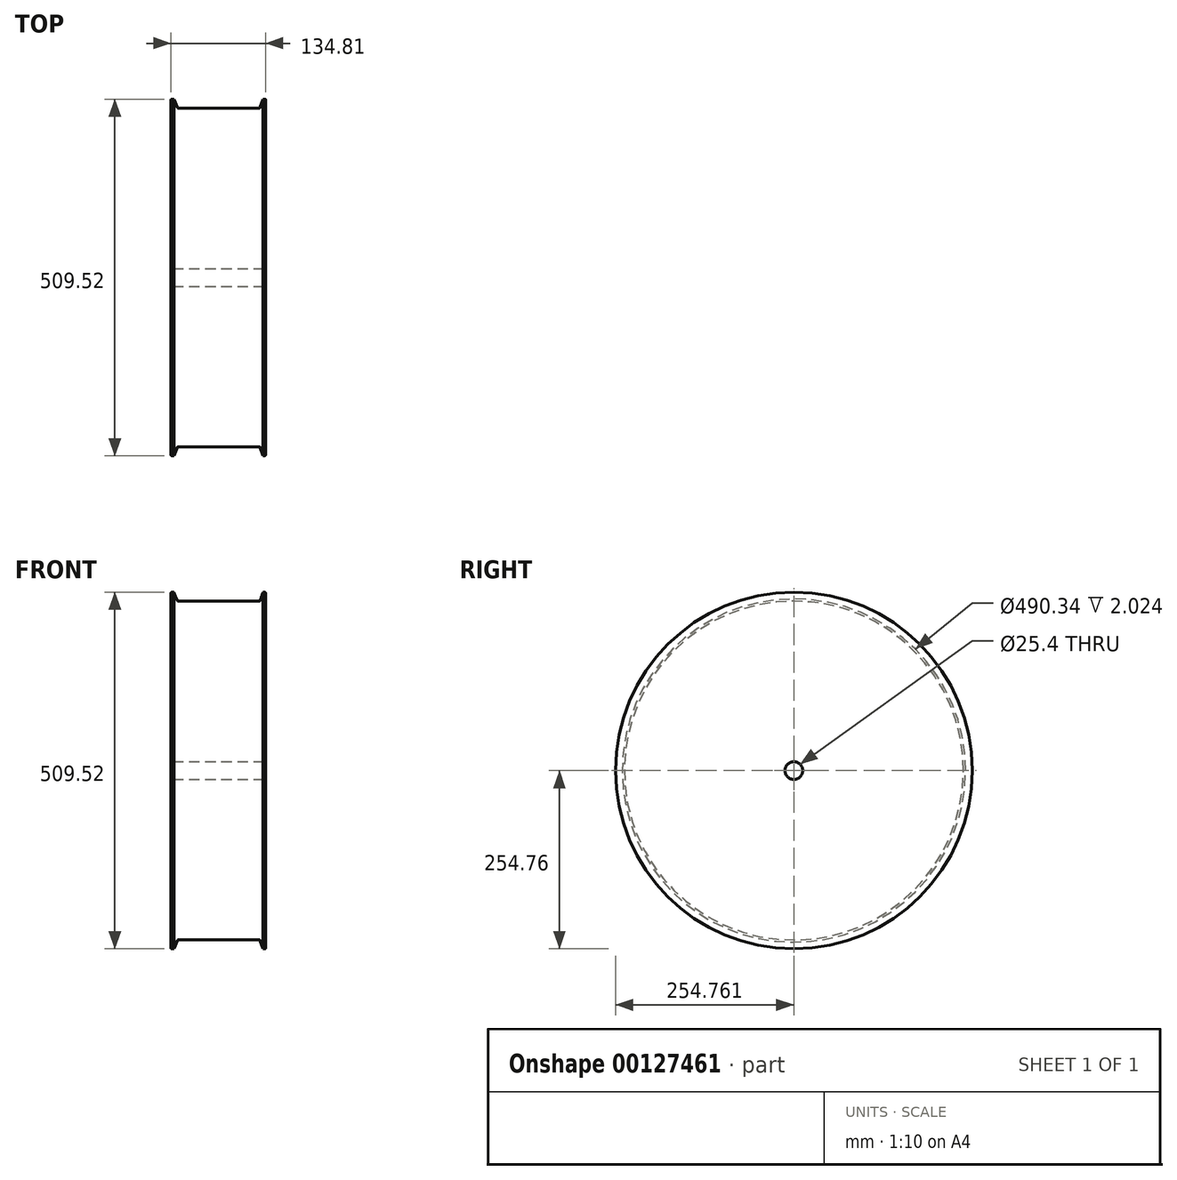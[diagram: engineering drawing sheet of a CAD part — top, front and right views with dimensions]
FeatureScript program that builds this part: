
annotation { "Feature Type Name" : "Feature", "Feature Type Description" : "" }
export const myFeature = defineFeature(function(context is Context, id is Id, definition is map)
    precondition{}
    {
        {
            var Q0;
            Q0=qCreatedBy(makeId("Top.planeOp"),FACE);
            var sketch = newSketch(context, id + "F0", { "sketchPlane" : qUnion([Q0])});
            skLineSegment(sketch, "E0", {"start": v(-3.62, 20.48) * mm, "end": v(-3.62, 29.09) * mm});
            skLineSegment(sketch, "E1", {"start": v(-2.86, 29.85) * mm, "end": v(0.66, 29.85) * mm});
            skLineSegment(sketch, "E2", {"start": v(0.66, 29.85) * mm, "end": v(5.74, 17.62) * mm});
            skArc(sketch, "E3.filletArc", {"start": v(-2.86, 29.85) * mm, "mid": v(-3.4, 29.62) * mm, "end": v(-3.62, 29.09) * mm});
            skLineSegment(sketch, "E4.0.MirrorCS", {"start": v(131.2, -224.69) * mm, "end": v(131.2, 29.31) * mm});
            skLineSegment(sketch, "E5", {"start": v(127.66, 30.07) * mm, "end": v(130.43, 30.07) * mm});
            skArc(sketch, "E6.filletArc", {"start": v(131.2, 29.31) * mm, "mid": v(130.97, 29.85) * mm, "end": v(130.43, 30.07) * mm});
            skLineSegment(sketch, "E7.0", {"start": v(-0.84, -224.69) * mm, "end": v(-0.84, 19.72) * mm});
            skLineSegment(sketch, "E8", {"start": v(-0.84, -224.69) * mm, "end": v(131.2, -224.69) * mm});
            skLineSegment(sketch, "E9.0.MirrorCS", {"start": v(127.66, 30.07) * mm, "end": v(123.34, 17.64) * mm});
            skLineSegment(sketch, "E10.0", {"start": v(6.1, 17.37) * mm, "end": v(122.97, 17.37) * mm});
            skLineSegment(sketch, "E11", {"start": v(-1.6, 20.48) * mm, "end": v(-3.62, 20.48) * mm});
            skPoint(sketch, "E12.visualSharp", {"position": v(-0.84, 20.48) * mm});
            skArc(sketch, "E12.filletArc", {"start": v(-0.84, 19.72) * mm, "mid": v(-1.06, 20.26) * mm, "end": v(-1.6, 20.48) * mm});
            skPoint(sketch, "E13.visualSharp", {"position": v(5.84, 17.37) * mm});
            skArc(sketch, "E13.filletArc", {"start": v(5.74, 17.62) * mm, "mid": v(5.89, 17.44) * mm, "end": v(6.1, 17.37) * mm});
            skPoint(sketch, "E14.visualSharp", {"position": v(123.25, 17.37) * mm});
            skArc(sketch, "E14.filletArc", {"start": v(122.97, 17.37) * mm, "mid": v(123.2, 17.45) * mm, "end": v(123.34, 17.64) * mm});
            skSolve(sketch);
        }
        {
            var Q0;
            Q0=makeQuery(id+"F0.imprint","IMPRINT",FACE,{"disambiguationData":[TD([[makeQuery(id+"F0.imprint","IMPRINT",EDGE,{"derivedFrom":sQuery(id+"F0.wireOp",EDGE,"E0")}),-1.0]])]});
            var Q1;
            Q1=qSketchRegion(id+"F2",true);
            var Q2;
            Q2=sQuery(id+"F0.wireOp",EDGE,"E8");
            revolve(context, id + "F1", {"entities" : qUnion([Q0, Q1]), "axis" : qUnion([Q2]), "revolveType" : RevolveType.FULL});
        }
        {
            var Q0;
            Q0=makeQuery(id+"F1.opRevolve","SWEPT_FACE",FACE,{"disambiguationData":[OSD([sQuery(id+"F0.wireOp",EDGE,"E4.0.MirrorCS")])]});
            var sketch = newSketch(context, id + "F2", { "sketchPlane" : qUnion([Q0])});
            skCircle(sketch, "E15", {"center": v(-224.69, 0) * mm, "radius": 12.7 * mm});
            skSolve(sketch);
        }
        {
            var Q0;
            Q0=makeQuery(id+"F2.imprint","IMPRINT",FACE,{"disambiguationData":[TD([[makeQuery(id+"F2.imprint","IMPRINT",EDGE,{"derivedFrom":sQuery(id+"F2.wireOp",EDGE,"E15")}),1.0]])]});
            extrude(context, id + "F3", {"entities" : qUnion([Q0]), "operationType" : NewBodyOperationType.REMOVE, "endBound" : BoundingType.THROUGH_ALL, "oppositeDirection" : true, "depth" : 11.1 * mm});
        }
    });
